# Revit family: 1. Вентиляторы UTR V1
name_source: partatom
category: Оборудование
revit_build: Autodesk Revit 2016 (Build: 20151209_0715(x64)
units: mm (PartAtom-declared; Revit-internal decimal feet)

## family parameters
Всегда вертикально = Да
На основе рабочей плоскости = Нет
Общий = Нет
При загрузке вырезать с полостями = Нет
Размер круглого соединителя = Использовать диаметр
Тип детали = Нормальный
Точка расчета площади = Нет

## types (23) — shared parameters
h = 60 мм
Единица измерения = шт.
Завод изготовитель = KORF
Ключевая пометка = Вентиляция
Наименование и тех.хар-ка = Радиальный вентилятор с назад загнутыми лопатками выхлоп прямо
Раздел = ОВ
Синий = Синий
высота ножек = 50 мм

## per-type parameters (varying)
| type | А | А1 | Б | Б1 | Г | Д | Д1 | Масса единицы | Материал | Мощность двигателя N,Вт | Напряжение U,В | Сила тока J, А | Тип, марка, обозначение | Частота вращения n, об/мин | высота | размер В | ширина |
| 50-25/22 | 710 мм | 690 мм | 470 мм | 450 мм | 395 мм | 510 мм | 490 мм | 43 | RAL 0000 Серый металл | 370 | 3х220/3х380 | 1,66/0,96 | UTR 50-25V1. 22-0,37x27(R) | 2730 | 250 мм | 635 мм | 500 мм |
| 50-25/25 | 710 мм | 690 мм | 470 мм | 450 мм | 395 мм | 510 мм | 490 мм | 45 | Сталь серая | 550 | 3х220/3х380 | 2,47/1,43 | UTR 50-25V1. 25-0,55x27(R) | 2730 | 250 мм | 635 мм | 500 мм |
| 50-30/25 | 710 мм | 690 мм | 520 мм | 500 мм | 445 мм | 510 мм | 490 мм | 47 | Сталь серая | 550 | 3х220/3х380 | 2,47/1,43 | UTR 50-30V1. 25-0,55x27(R) | 2730 | 300 мм | 635 мм | 500 мм |
| 50-30/28 | 710 мм | 690 мм | 520 мм | 500 мм | 445 мм | 710 мм | 690 мм | 54 | Сталь серая | 1100 | 3х220/3х380 | 4,4/2,52 | UTR 50-30V1. 28-1,1x28(R) | 2800 | 300 мм | 635 мм | 500 мм |
| 50-30/31 | 710 мм | 690 мм | 520 мм | 500 мм | 445 мм | 710 мм | 690 мм | 54 | Сталь серая | 1100 | 3х220/3х380 | 4,4/2,52 | UTR 50-30V1.31-1,1x28(R) | 2800 | 300 мм | 635 мм | 500 мм |
| 60-30/28 | 810 мм | 790 мм | 520 мм | 500 мм | 445 мм | 710 мм | 690 мм | 58 | Сталь серая | 1100 | 3х220/3х380 | 4,4/2,52 | UTR 60-30V1.28-1,1x28(R) | 2800 | 300 мм | 735 мм | 600 мм |
| 60-30/31 | 810 мм | 790 мм | 520 мм | 500 мм | 445 мм | 710 мм | 690 мм | 58 | Сталь серая | 1100 | 3х220/3х380 | 4,4/2,52 | UTR 60-30V1.31-1,1x28(R) | 2800 | 300 мм | 735 мм | 600 мм |
| 60-35/31 | 810 мм | 790 мм | 570 мм | 550 мм | 495 мм | 610 мм | 590 мм | 60 | Сталь серая | 1100 | 3х220/3х380 | 4,4/2,52 | UTR 60-35V1.31-1,1x28(R) | 2800 | 350 мм | 735 мм | 600 мм |
| 60-35/31-1,5 | 810 мм | 790 мм | 570 мм | 550 мм | 495 мм | 610 мм | 590 мм | 63 | Сталь серая | 1500 | 3х220/3х380 | 5,6/3,3 | UTR 60-35V1.31-1,5x28(R) | 2880 | 350 мм | 735 мм | 600 мм |
| 60-35/35 | 810 мм | 790 мм | 570 мм | 550 мм | 495 мм | 610 мм | 590 мм | 70 | Сталь серая | 2200 | 3х220/3х380 | 8,0/4,6 | UTR 60-35V1.35-2,2x28(R) | 2860 | 350 мм | 735 мм | 600 мм |
| 70-40/31 | 910 мм | 890 мм | 620 мм | 600 мм | 545 мм | 610 мм | 590 мм | 66 | Сталь серая | 1100 | 3х220/3х380 | 4,4/2,52 | UTR 70-40V1.31-1,1x28(R) | 2800 | 400 мм | 835 мм | 700 мм |
| 70-40/31-2,2 | 910 мм | 890 мм | 620 мм | 600 мм | 545 мм | 710 мм | 690 мм | 75 | Сталь серая | 2200 | 3х220/3х380 | 8,0/4,6 | UTR 70-40V1.31-2,2x28(R) | 2860 | 400 мм | 835 мм | 700 мм |
| 70-40/35 | 910 мм | 890 мм | 620 мм | 600 мм | 545 мм | 710 мм | 690 мм | 75 | Сталь серая | 2200 | 3х220/3х380 | 8,0/4,6 | UTR 70-40V1.35-2,2x28(R) | 2860 | 400 мм | 835 мм | 700 мм |
| 80-50/35 | 1010 мм | 990 мм | 720 мм | 700 мм | 645 мм | 710 мм | 690 мм | 84 | Сталь серая | 2200 | 3х220/3х380 | 8,0/4,6 | UTR 80-50V1.35-2,2x28(R) | 2860 | 500 мм | 935 мм | 800 мм |
| 80-50/35-3,0 | 1010 мм | 990 мм | 720 мм | 700 мм | 645 мм | 710 мм | 690 мм | 88 | Сталь серая | 3000 | 3х220/3х380 | 10,5/6,0 | UTR 80-50V1.35-3,0x28(R) | 2860 | 500 мм | 935 мм | 800 мм |
| 80-50/40 | 1010 мм | 990 мм | 720 мм | 700 мм | 645 мм | 840 мм | 820 мм | 105 | Сталь серая | 4000 | 3х380/3х660 | 8,0/4,6 | UTR 80-50V1.40-4,0x28(R) | 2850 | 500 мм | 935 мм | 800 мм |
| 90-50/35 | 1125 мм | 1105 мм | 740 мм | 720 мм | 665 мм | 730 мм | 710 мм | 96 | Сталь серая | 3000 | 3х220/3х380 | 10,5/6,0 | UTR 90-50V1.35-3,0x28(R) | 2860 | 500 мм | 1050 мм | 900 мм |
| 90-50/40 | 1125 мм | 1105 мм | 740 мм | 720 мм | 665 мм | 840 мм | 820 мм | 111 | Сталь серая | 4000 | 3х380/3х660 | 8,0/4,6 | UTR 90-50V1.40-4,0x28(R) | 2850 | 500 мм | 1050 мм | 900 мм |
| 90-50/45 | 1125 мм | 1105 мм | 740 мм | 720 мм | 665 мм | 840 мм | 820 мм | 112 | Сталь серая | 3000 | 3х220/3х380 | 11,6/6,7 | UTR 90-50V1.45-3,0x14(R) | 1410 | 500 мм | 1050 мм | 900 мм |
| 100-50/40 | 1225 мм | 1205 мм | 740 мм | 720 мм | 665 мм | 840 мм | 820 мм | 117 | Сталь серая | 4000 | 3х380/3х660 | 8,0/4,6 | UTR 100-50V1.40-4,0x28(R) | 2850 | 500 мм | 1150 мм | 1000 мм |
| 100-50/45 | 1225 мм | 1205 мм | 740 мм | 720 мм | 665 мм | 840 мм | 820 мм | 116 | Сталь серая | 3000 | 3х220/3х380 | 11,6/6,7 | UTR 100-50V1.45-3,0x14(R) | 1410 | 500 мм | 1150 мм | 1000 мм |
| 100-50/45-4,0 | 1225 мм | 1205 мм | 740 мм | 720 мм | 665 мм | 840 мм | 820 мм | 124 | Сталь серая | 4000 | 3х380/3х660 | 8,5/4,9 | UTR 100-50V1.45-4,0x14(R) | 1410 | 500 мм | 1150 мм | 1000 мм |
| 100-50/45-5,5 | 1225 мм | 1205 мм | 740 мм | 720 мм | 665 мм | 840 мм | 820 мм | 133 | Сталь серая | 4000 | 3х380/3х660 | 11,0/6,5 | UTR 100-50V1.45-5,5x14(R) | 1430 | 500 мм | 1150 мм | 1000 мм |
